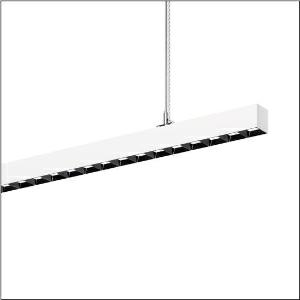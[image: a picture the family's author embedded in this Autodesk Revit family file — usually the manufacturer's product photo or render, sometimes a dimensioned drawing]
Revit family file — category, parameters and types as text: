
# Revit family: silica_r__21_51mx32tat7w_976d
name_source: partatom
category: Lighting Fixtures
units: mm (PartAtom-declared; Revit-internal decimal feet)

## family parameters
Cut with Voids When Loaded = No
Host = Face
Light Source = No
Part Type = Normal
Room Calculation Point = No
Round Connector Dimension = Use Diameter
Shared = No

## types (1)
- --- (1 x LED, 6220 lm, 53.4 W, 6500K)
    Apparent Load = 53 VA
    CIE Flux Codes = 84 99 100 60 100
    Color Rendering = 80
    Color Temperature = 6500K
    Default Elevation = 1800 mm
    Description = Silica® 21, office luminaire, primary light control with darklight reflector, of PMMA, black, CAT 2 (L<= 3000cd/m²), light emission: direct/indirect distribution, primary light characteristic: symmetric, installation type: suspended mounting, LED, rated luminous flux: 6.220lm, luminous efficacy: 111lm/W, light colour: 8tw, colour temperature: 2700..6500K, control gear: ECG DALI, with terminal, 3+2-pole, max. 2.5mm², mains connection: 220..240V, AC, 50/60Hz, rated input power: 56.1W, luminaire housing, of aluminium, traffic white (RAL 9016), length: 1.204mm, width: 53mm, height: 53mm, protection rating (complete): IP20, insulation class (complete): insulation class I (protective earthing), certification: CE, permissible operating ambient temperature: 0..+35°C, standard: EN 50419, packaging unit: 1 piece
    Height = 53 mm
    Lamp = 1 x LED
    Lamp Light Flux = 6220 lm
    Lamp Power = 53.4 W
    Lamp count = 1
    Length = 1204 mm
    Luminous efficacy = 116 lm/W
    Manufacturer = Siteco
    ModVariant = No
    Model = 51MX32TAT7W
    Mounting Place = Ceiling
    Mounting Type = Pendant
    Number of Poles = 1
    OnlyDefault = Yes
    Power Factor = 1
    Product Name = Silica® 21
    Product group = office luminaire | ceiling pendant
    ProductGroupID = 902
    Protection Class = Protection class I
    Protection Degree = IP 20
    RLX_Detail_Level = 1
    RLX_Emergency_Light_Flux = 0 lm
    RLX_Emergency_Type = 0
    RLX_Emergency_Type_DB = No
    RlxData = <blob elided: 40429 chars, md5=7ba5f132>
    Socket = socket
    Standby Power = 0 W
    System Light Flux = 6220 lm
    System Power = 53 W
    Type Comments = individual setting
    Type Image = l_1313619.jpg
    URL = http://relux.com
    VarID = @adj_089331
    Voltage = 0 V
    Weight = 0.00 kg
    Width = 53 mm

## geometry (parser evidence)
native form markers: Blend x4, Sweep x11
no freeform markers — native parametric forms only
